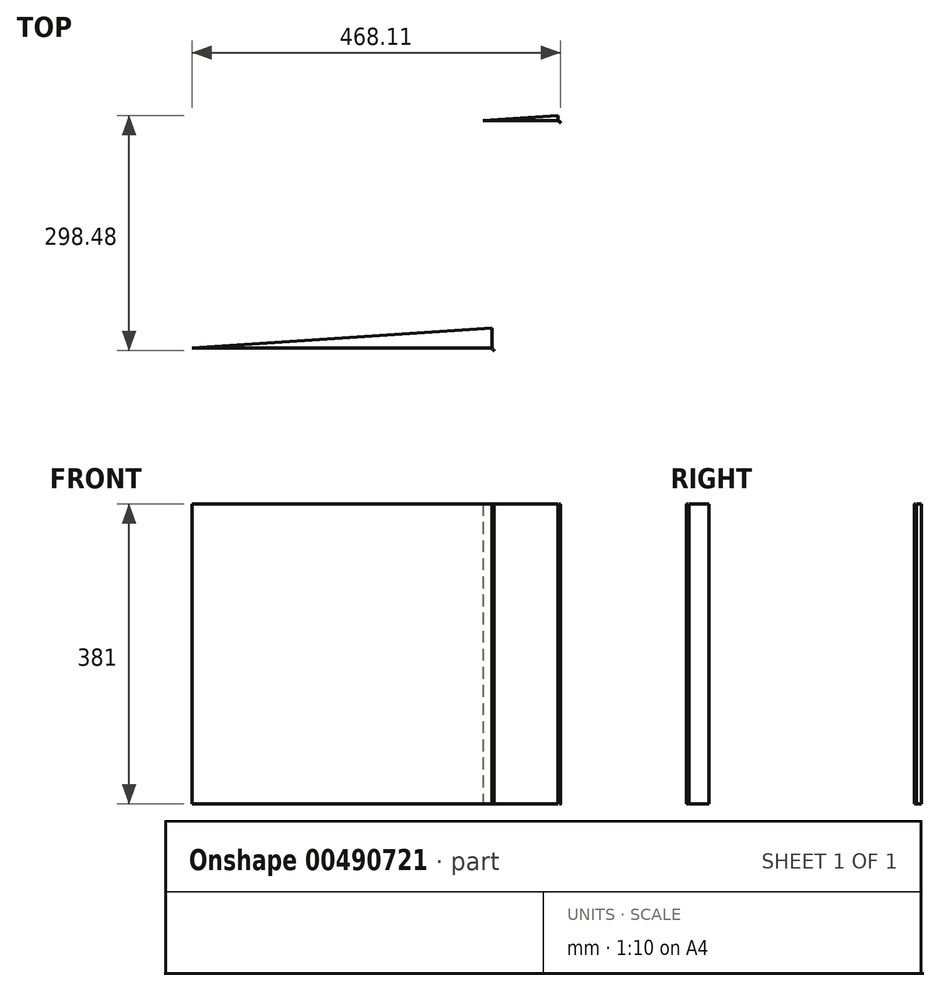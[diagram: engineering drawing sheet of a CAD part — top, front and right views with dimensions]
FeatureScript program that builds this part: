
annotation { "Feature Type Name" : "Feature", "Feature Type Description" : "" }
export const myFeature = defineFeature(function(context is Context, id is Id, definition is map)
    precondition{}
    {
        {
            var Q0;
            Q0=qCreatedBy(makeId("Top.planeOp"),FACE);
            var sketch = newSketch(context, id + "F0", { "sketchPlane" : qUnion([Q0])});
            skLineSegment(sketch, "E0", {"start": v(-167.3, -43.6) * mm, "end": v(213.7, -43.6) * mm});
            skLineSegment(sketch, "E1", {"start": v(213.7, -43.6) * mm, "end": v(213.7, -18.2) * mm});
            skLineSegment(sketch, "E2", {"start": v(213.7, -18.2) * mm, "end": v(-167.3, -43.6) * mm});
            skLineSegment(sketch, "E3", {"start": v(246.53, 229.21) * mm, "end": v(246.53, 229.21) * mm});
            skLineSegment(sketch, "E4", {"start": v(202.5, 245.12) * mm, "end": v(297.76, 245.12) * mm});
            skLineSegment(sketch, "E5", {"start": v(297.76, 245.12) * mm, "end": v(297.76, 251.47) * mm});
            skLineSegment(sketch, "E6", {"start": v(297.76, 251.47) * mm, "end": v(202.5, 245.12) * mm});
            skCircle(sketch, "E7", {"center": v(215.67, -46.22) * mm, "radius": 0.8 * mm});
            skCircle(sketch, "E8", {"center": v(300.01, 243.3) * mm, "radius": 0.8 * mm});
            skSolve(sketch);
        }
        {
            var Q0;
            Q0 = qSketchRegion(id + "F0", true);
            extrude(context, id + "F1", {"entities" : qUnion([Q0]), "depth" : 381 * mm});
        }
    });
